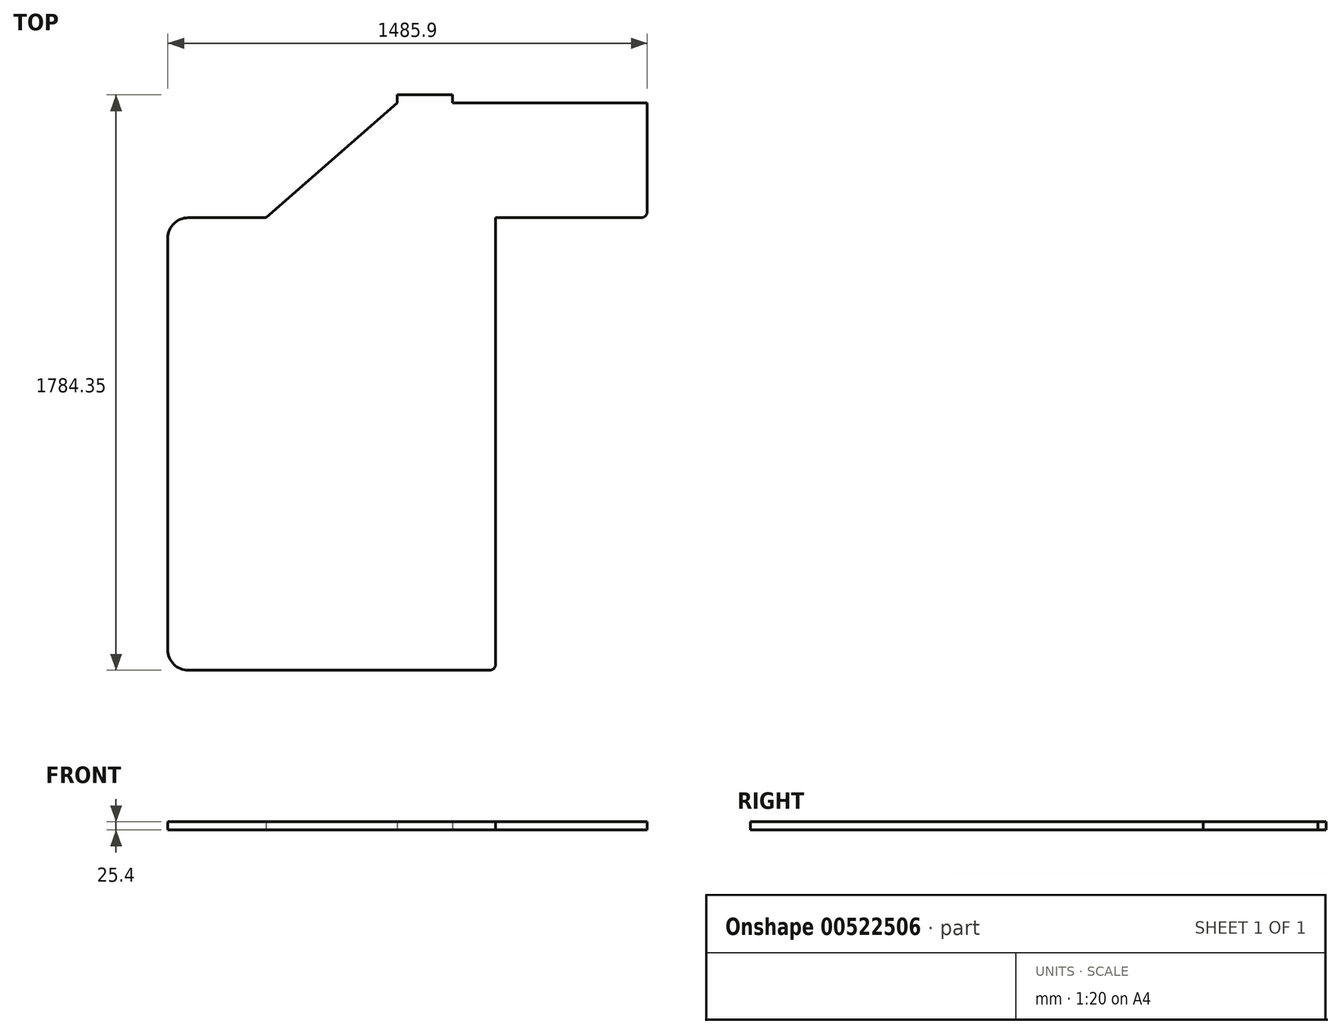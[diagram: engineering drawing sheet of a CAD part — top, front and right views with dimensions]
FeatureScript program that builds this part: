
annotation { "Feature Type Name" : "Feature", "Feature Type Description" : "" }
export const myFeature = defineFeature(function(context is Context, id is Id, definition is map)
    precondition{}
    {
        {
            var Q0;
            Q0=qCreatedBy(makeId("Top.planeOp"),FACE);
            var sketch = newSketch(context, id + "F0", { "sketchPlane" : qUnion([Q0])});
            skLineSegment(sketch, "E0", {"start": v(0, 1354.96) * mm, "end": v(0, 63.5) * mm});
            skLineSegment(sketch, "E1", {"start": v(63.5, 0) * mm, "end": v(996.95, 0) * mm});
            skLineSegment(sketch, "E2", {"start": v(1016, 19.05) * mm, "end": v(1016, 1403.35) * mm});
            skLineSegment(sketch, "E3", {"start": v(1016, 1403.35) * mm, "end": v(1466.85, 1403.35) * mm});
            skLineSegment(sketch, "E4", {"start": v(1485.9, 1422.4) * mm, "end": v(1485.9, 1758.95) * mm});
            skLineSegment(sketch, "E5", {"start": v(1485.9, 1758.95) * mm, "end": v(882.65, 1758.95) * mm});
            skLineSegment(sketch, "E6", {"start": v(711.2, 1758.95) * mm, "end": v(711.2, 1784.35) * mm});
            skLineSegment(sketch, "E7", {"start": v(711.2, 1784.35) * mm, "end": v(882.65, 1784.35) * mm});
            skLineSegment(sketch, "E8", {"start": v(882.65, 1784.35) * mm, "end": v(882.65, 1758.95) * mm});
            skPoint(sketch, "E9.visualSharp", {"position": v(1485.9, 1403.35) * mm});
            skArc(sketch, "E9.filletArc", {"start": v(1466.85, 1403.35) * mm, "mid": v(1480.32, 1408.93) * mm, "end": v(1485.9, 1422.4) * mm});
            skPoint(sketch, "E10.visualSharp", {"position": v(1016, 0) * mm});
            skArc(sketch, "E10.filletArc", {"start": v(996.95, 0) * mm, "mid": v(1010.42, 5.58) * mm, "end": v(1016, 19.05) * mm});
            skPoint(sketch, "E11.visualSharp", {"position": v(0, 0) * mm});
            skArc(sketch, "E11.filletArc", {"start": v(0, 63.5) * mm, "mid": v(18.6, 18.6) * mm, "end": v(63.5, 0) * mm});
            skLineSegment(sketch, "E12.bottom", {"start": v(990.6, 25.4) * mm, "end": v(342.9, 25.4) * mm, "construction": true});
            skLineSegment(sketch, "E12.top", {"start": v(990.6, 1403.35) * mm, "end": v(342.9, 1403.35) * mm, "construction": true});
            skLineSegment(sketch, "E12.left", {"start": v(990.6, 25.4) * mm, "end": v(990.6, 1403.35) * mm, "construction": true});
            skLineSegment(sketch, "E12.right", {"start": v(342.9, 25.4) * mm, "end": v(342.9, 1403.35) * mm, "construction": true});
            skLineSegment(sketch, "E13", {"start": v(711.2, 1758.95) * mm, "end": v(304.8, 1403.35) * mm});
            skLineSegment(sketch, "E14", {"start": v(304.8, 1403.35) * mm, "end": v(63.5, 1403.35) * mm});
            skLineSegment(sketch, "E15", {"start": v(0, 1354.96) * mm, "end": v(0, 1339.85) * mm});
            skPoint(sketch, "E16.visualSharp", {"position": v(0, 1403.35) * mm});
            skArc(sketch, "E16.filletArc", {"start": v(63.5, 1403.35) * mm, "mid": v(18.6, 1384.75) * mm, "end": v(0, 1339.85) * mm});
            skSolve(sketch);
        }
        {
            var Q0;
            Q0=makeQuery(id+"F0.imprint","IMPRINT",FACE,{"disambiguationData":[TD([[makeQuery(id+"F0.imprint","IMPRINT",EDGE,{"derivedFrom":sQuery(id+"F0.wireOp",EDGE,"E0")}),1.0]])]});
            extrude(context, id + "F1", {"entities" : qUnion([Q0]), "depth" : 25.4 * mm, "offsetDistance" : 25.4 * mm});
        }
    });
